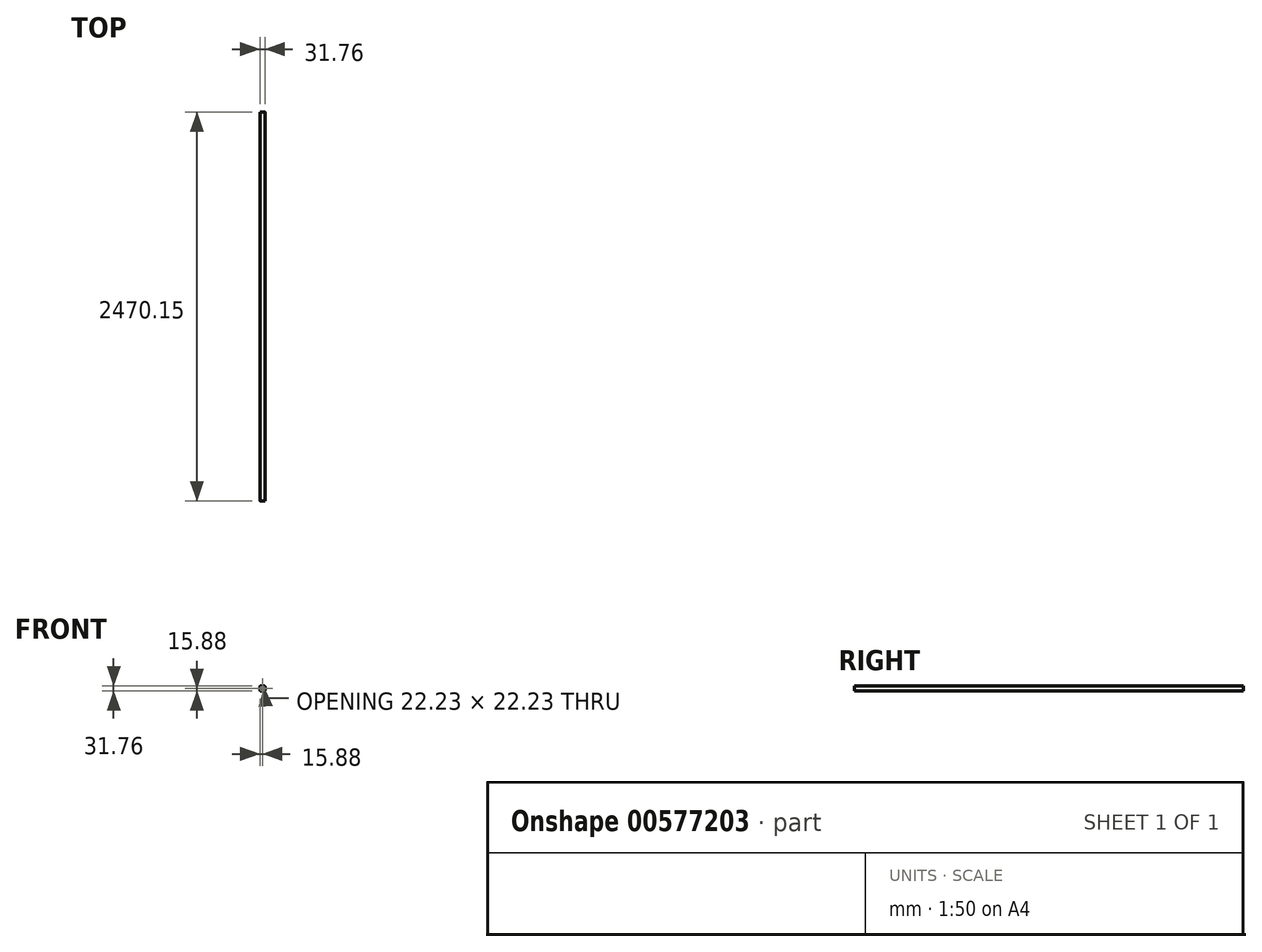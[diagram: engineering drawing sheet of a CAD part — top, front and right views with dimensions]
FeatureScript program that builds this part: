
annotation { "Feature Type Name" : "Feature", "Feature Type Description" : "" }
export const myFeature = defineFeature(function(context is Context, id is Id, definition is map)
    precondition{}
    {
        {
            var Q0;
            Q0=qCreatedBy(makeId("Front.planeOp"),FACE);
            var sketch = newSketch(context, id + "F0", { "sketchPlane" : qUnion([Q0])});
            skLineSegment(sketch, "E0.bottom", {"start": v(12.7, 15.88) * mm, "end": v(-12.7, 15.88) * mm});
            skLineSegment(sketch, "E0.top", {"start": v(12.7, -15.87) * mm, "end": v(-12.7, -15.87) * mm});
            skLineSegment(sketch, "E0.left", {"start": v(15.88, 12.7) * mm, "end": v(15.88, -12.7) * mm});
            skLineSegment(sketch, "E0.right", {"start": v(-15.88, 12.7) * mm, "end": v(-15.88, -12.7) * mm});
            skPoint(sketch, "E0.middle", {"position": v(0, 0) * mm});
            skLineSegment(sketch, "E1.bottom", {"start": v(7.94, 11.11) * mm, "end": v(-7.94, 11.11) * mm});
            skLineSegment(sketch, "E1.top", {"start": v(7.94, -11.11) * mm, "end": v(-7.94, -11.11) * mm});
            skLineSegment(sketch, "E1.left", {"start": v(11.11, 7.94) * mm, "end": v(11.11, -7.94) * mm});
            skLineSegment(sketch, "E1.right", {"start": v(-11.11, 7.94) * mm, "end": v(-11.11, -7.94) * mm});
            skPoint(sketch, "E2.visualSharp", {"position": v(-15.88, 15.87) * mm});
            skArc(sketch, "E2.filletArc", {"start": v(-12.7, 15.87) * mm, "mid": v(-14.95, 14.95) * mm, "end": v(-15.88, 12.7) * mm});
            skPoint(sketch, "E3.visualSharp", {"position": v(-11.11, 11.11) * mm});
            skArc(sketch, "E3.filletArc", {"start": v(-7.94, 11.11) * mm, "mid": v(-10.18, 10.18) * mm, "end": v(-11.11, 7.94) * mm});
            skPoint(sketch, "E4.visualSharp", {"position": v(15.88, 15.88) * mm});
            skArc(sketch, "E4.filletArc", {"start": v(15.88, 12.7) * mm, "mid": v(14.95, 14.95) * mm, "end": v(12.7, 15.88) * mm});
            skPoint(sketch, "E5.visualSharp", {"position": v(11.11, 11.11) * mm});
            skArc(sketch, "E5.filletArc", {"start": v(11.11, 7.94) * mm, "mid": v(10.18, 10.18) * mm, "end": v(7.94, 11.11) * mm});
            skPoint(sketch, "E6.visualSharp", {"position": v(11.11, -11.11) * mm});
            skArc(sketch, "E6.filletArc", {"start": v(7.94, -11.11) * mm, "mid": v(10.18, -10.18) * mm, "end": v(11.11, -7.94) * mm});
            skPoint(sketch, "E7.visualSharp", {"position": v(-11.11, -11.11) * mm});
            skArc(sketch, "E7.filletArc", {"start": v(-11.11, -7.94) * mm, "mid": v(-10.18, -10.18) * mm, "end": v(-7.94, -11.11) * mm});
            skPoint(sketch, "E8.visualSharp", {"position": v(15.88, -15.87) * mm});
            skArc(sketch, "E8.filletArc", {"start": v(12.7, -15.87) * mm, "mid": v(14.95, -14.95) * mm, "end": v(15.88, -12.7) * mm});
            skPoint(sketch, "E9.visualSharp", {"position": v(-15.88, -15.88) * mm});
            skArc(sketch, "E9.filletArc", {"start": v(-15.88, -12.7) * mm, "mid": v(-14.95, -14.95) * mm, "end": v(-12.7, -15.88) * mm});
            skSolve(sketch);
        }
        {
            var Q0;
            Q0 = qSketchRegion(id + "F0", true);
            extrude(context, id + "F1", {"entities" : qUnion([Q0]), "oppositeDirection" : true, "depth" : 2470.15 * mm, "offsetDistance" : 25.4 * mm});
        }
    });
